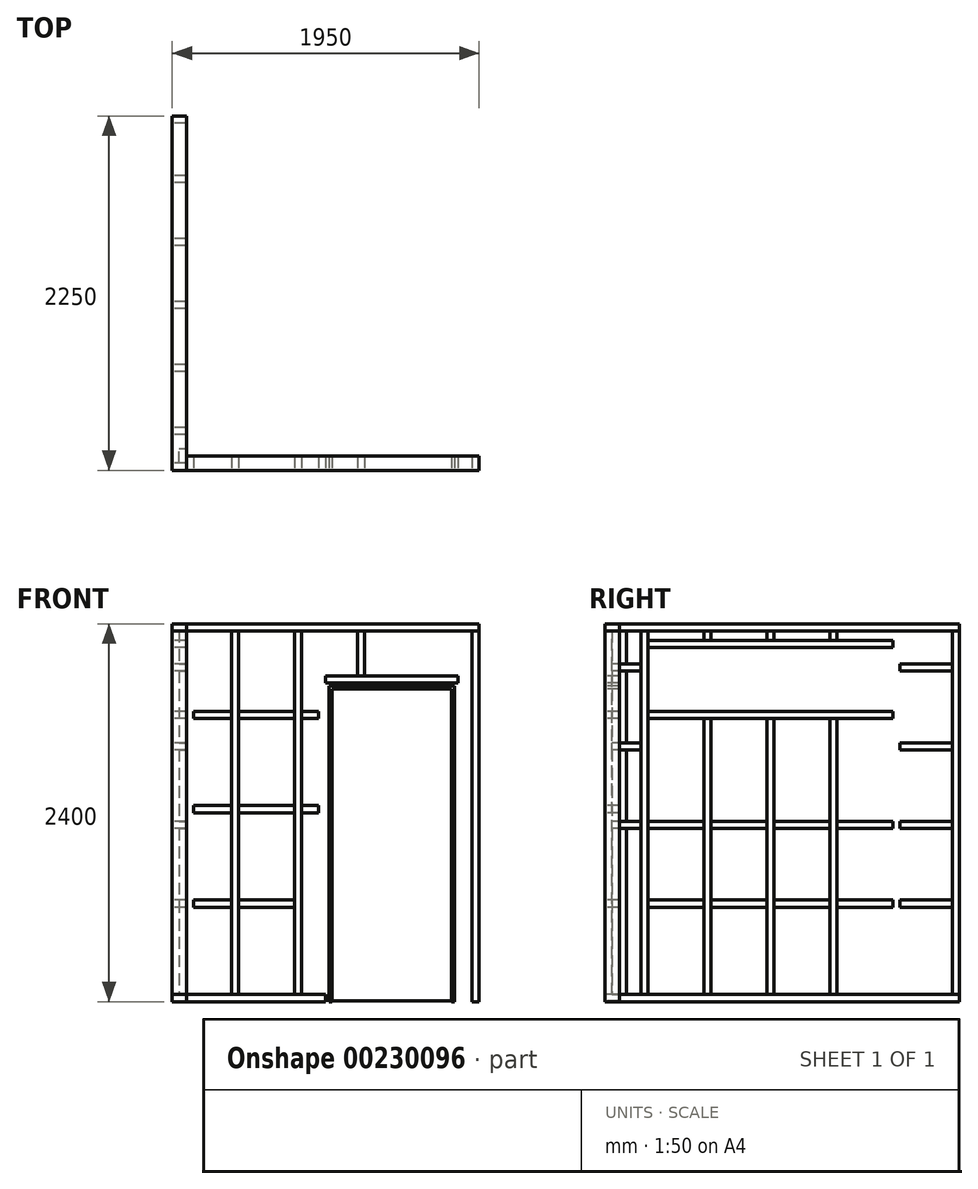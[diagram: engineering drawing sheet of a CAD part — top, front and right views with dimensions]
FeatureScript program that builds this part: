
annotation { "Feature Type Name" : "Feature", "Feature Type Description" : "" }
export const myFeature = defineFeature(function(context is Context, id is Id, definition is map)
    precondition{}
    {
        {
            var Q0;
            Q0=qCreatedBy(makeId("Top.planeOp"),FACE);
            var sketch = newSketch(context, id + "F0", { "sketchPlane" : qUnion([Q0])});
            skLineSegment(sketch, "E0.bottom", {"start": v(-1950, 0) * mm, "end": v(0, 0) * mm});
            skLineSegment(sketch, "E0.top", {"start": v(-1950, -2250) * mm, "end": v(0, -2250) * mm});
            skLineSegment(sketch, "E0.left", {"start": v(-1950, 0) * mm, "end": v(-1950, -2250) * mm});
            skLineSegment(sketch, "E0.right", {"start": v(0, 0) * mm, "end": v(0, -2250) * mm});
            skLineSegment(sketch, "E1.bottom", {"start": v(-1950, 0) * mm, "end": v(-1860, 0) * mm});
            skLineSegment(sketch, "E1.top", {"start": v(-1950, -2250) * mm, "end": v(-1860, -2250) * mm});
            skLineSegment(sketch, "E1.right", {"start": v(-1860, 0) * mm, "end": v(-1860, -2250) * mm});
            skLineSegment(sketch, "E2.bottom", {"start": v(-1860, -2160) * mm, "end": v(0, -2160) * mm});
            skLineSegment(sketch, "E2.top", {"start": v(-1860, -2250) * mm, "end": v(0, -2250) * mm});
            skLineSegment(sketch, "E2.left", {"start": v(-1860, -2160) * mm, "end": v(-1860, -2250) * mm});
            skLineSegment(sketch, "E2.right", {"start": v(0, -2160) * mm, "end": v(0, -2250) * mm});
            skSolve(sketch);
        }
        {
            var Q0;
            Q0=qCreatedBy(makeId("Right.planeOp"),FACE);
            var Q1;
            Q1=sQuery(id+"F0.wireOp",VERTEX,"E0.bottom.start");
            cPlane(context, id + "F1", {"entities" : qUnion([Q0, Q1]), "cplaneType" : CPlaneType.PLANE_POINT, "offset" : 25 * mm, "width" : 150 * mm, "height" : 150 * mm});
        }
        {
            var Q0;
            Q0=qCreatedBy(makeId("Front.planeOp"),FACE);
            var Q1;
            Q1=sQuery(id+"F0.wireOp",VERTEX,"E0.top.end");
            cPlane(context, id + "F2", {"entities" : qUnion([Q0, Q1]), "cplaneType" : CPlaneType.PLANE_POINT, "offset" : 25 * mm, "width" : 150 * mm, "height" : 150 * mm});
        }
        {
            var Q0;
            Q0=qCreatedBy(id+"F1.planeOp",FACE);
            var sketch = newSketch(context, id + "F3", { "sketchPlane" : qUnion([Q0])});
            skLineSegment(sketch, "E3.left", {"start": v(0, 0) * mm, "end": v(0, 2400) * mm});
            skLineSegment(sketch, "E4.0", {"start": v(-45, 45) * mm, "end": v(-45, 2355) * mm});
            skLineSegment(sketch, "E4.2", {"start": v(-2205, 45) * mm, "end": v(-2205, 2355) * mm});
            skLineSegment(sketch, "E5.left", {"start": v(-45, 645) * mm, "end": v(-45, 600) * mm});
            skLineSegment(sketch, "E6", {"start": v(-45, 45) * mm, "end": v(0, 45) * mm});
            skLineSegment(sketch, "E7", {"start": v(0, 2400) * mm, "end": v(-2250, 2400) * mm});
            skLineSegment(sketch, "E8", {"start": v(-45, 2355) * mm, "end": v(-2205, 2355) * mm});
            skLineSegment(sketch, "E9", {"start": v(-45, 2355) * mm, "end": v(0, 2355) * mm});
            skLineSegment(sketch, "E10", {"start": v(-2205, 2355) * mm, "end": v(-2250, 2355) * mm});
            skLineSegment(sketch, "E11", {"start": v(-2250, 0) * mm, "end": v(-2250, 2355) * mm});
            skLineSegment(sketch, "E12", {"start": v(-2250, 2400) * mm, "end": v(-2250, 2355) * mm});
            skLineSegment(sketch, "E13.bottom", {"start": v(-45, 45) * mm, "end": v(-2205, 45) * mm});
            skLineSegment(sketch, "E13.top", {"start": v(0, 0) * mm, "end": v(-2250, 0) * mm});
            skLineSegment(sketch, "E14.bottom", {"start": v(0, 45) * mm, "end": v(-45, 45) * mm});
            skLineSegment(sketch, "E14.left", {"start": v(0, 45) * mm, "end": v(0, 0) * mm});
            skLineSegment(sketch, "E15", {"start": v(-2205, 45) * mm, "end": v(-2250, 45) * mm});
            skLineSegment(sketch, "E16.bottom", {"start": v(-45, 645) * mm, "end": v(-377.5, 645) * mm});
            skLineSegment(sketch, "E16.top", {"start": v(-45, 600) * mm, "end": v(-377.5, 600) * mm});
            skLineSegment(sketch, "E16.right", {"start": v(-2205, 645) * mm, "end": v(-2205, 600) * mm});
            skLineSegment(sketch, "E17.bottom", {"start": v(-377.5, 45) * mm, "end": v(-422.5, 45) * mm});
            skLineSegment(sketch, "E17.top", {"start": v(-377.5, 2355) * mm, "end": v(-422.5, 2355) * mm});
            skLineSegment(sketch, "E17.left", {"start": v(-377.5, 45) * mm, "end": v(-377.5, 2355) * mm});
            skLineSegment(sketch, "E17.right", {"start": v(-422.5, 45) * mm, "end": v(-422.5, 2355) * mm});
            skPoint(sketch, "E18", {"position": v(-400, 45) * mm});
            skPoint(sketch, "E19", {"position": v(0, 45) * mm});
            skLineSegment(sketch, "E20.1.0.0", {"start": v(-777.5, 45) * mm, "end": v(-777.5, 1800) * mm});
            skLineSegment(sketch, "E20.1.0.1", {"start": v(-822.5, 45) * mm, "end": v(-822.5, 1800) * mm});
            skLineSegment(sketch, "E20.2.0.0", {"start": v(-1177.5, 45) * mm, "end": v(-1177.5, 1800) * mm});
            skLineSegment(sketch, "E20.2.0.1", {"start": v(-1222.5, 45) * mm, "end": v(-1222.5, 1800) * mm});
            skLineSegment(sketch, "E20.3.0.0", {"start": v(-1577.5, 45) * mm, "end": v(-1577.5, 1800) * mm});
            skLineSegment(sketch, "E20.3.0.1", {"start": v(-1622.5, 45) * mm, "end": v(-1622.5, 1800) * mm});
            skLineSegment(sketch, "E20.4.0.0", {"start": v(-1977.5, 45) * mm, "end": v(-1977.5, 2355) * mm});
            skLineSegment(sketch, "E20.4.0.1", {"start": v(-2022.5, 45) * mm, "end": v(-2022.5, 2355) * mm});
            skLineSegment(sketch, "E20.direction1", {"start": v(-422.5, 45) * mm, "end": v(-822.5, 45) * mm, "construction": true});
            skLineSegment(sketch, "E21.trimOffspring", {"start": v(-422.5, 645) * mm, "end": v(-777.5, 645) * mm});
            skLineSegment(sketch, "E22.trimOffspring", {"start": v(-422.5, 600) * mm, "end": v(-777.5, 600) * mm});
            skLineSegment(sketch, "E23.trimOffspring", {"start": v(-822.5, 645) * mm, "end": v(-1177.5, 645) * mm});
            skLineSegment(sketch, "E24.trimOffspring", {"start": v(-822.5, 600) * mm, "end": v(-1177.5, 600) * mm});
            skLineSegment(sketch, "E25.trimOffspring", {"start": v(-1222.5, 645) * mm, "end": v(-1577.5, 645) * mm});
            skLineSegment(sketch, "E26.trimOffspring", {"start": v(-1222.5, 600) * mm, "end": v(-1577.5, 600) * mm});
            skLineSegment(sketch, "E27.trimOffspring", {"start": v(-1622.5, 645) * mm, "end": v(-1977.5, 645) * mm});
            skLineSegment(sketch, "E28.trimOffspring", {"start": v(-1622.5, 600) * mm, "end": v(-1977.5, 600) * mm});
            skLineSegment(sketch, "E29.trimOffspring", {"start": v(-2022.5, 645) * mm, "end": v(-2205, 645) * mm});
            skLineSegment(sketch, "E30.trimOffspring", {"start": v(-2022.5, 600) * mm, "end": v(-2205, 600) * mm});
            skLineSegment(sketch, "E31.0.1.0", {"start": v(-822.5, 1100) * mm, "end": v(-1177.5, 1100) * mm});
            skLineSegment(sketch, "E31.0.1.1", {"start": v(-422.5, 1100) * mm, "end": v(-777.5, 1100) * mm});
            skLineSegment(sketch, "E31.0.1.2", {"start": v(-422.5, 1145) * mm, "end": v(-777.5, 1145) * mm});
            skLineSegment(sketch, "E31.0.1.3", {"start": v(-822.5, 1145) * mm, "end": v(-1177.5, 1145) * mm});
            skLineSegment(sketch, "E31.0.1.4", {"start": v(-2022.5, 1145) * mm, "end": v(-2205, 1145) * mm});
            skLineSegment(sketch, "E31.0.1.5", {"start": v(-45, 1145) * mm, "end": v(-377.5, 1145) * mm});
            skLineSegment(sketch, "E31.0.1.6", {"start": v(-1622.5, 1100) * mm, "end": v(-1977.5, 1100) * mm});
            skLineSegment(sketch, "E31.0.1.7", {"start": v(-1222.5, 1100) * mm, "end": v(-1577.5, 1100) * mm});
            skLineSegment(sketch, "E31.0.1.8", {"start": v(-1622.5, 1145) * mm, "end": v(-1977.5, 1145) * mm});
            skLineSegment(sketch, "E31.0.1.9", {"start": v(-1222.5, 1145) * mm, "end": v(-1577.5, 1145) * mm});
            skLineSegment(sketch, "E31.0.1.10", {"start": v(-45, 1100) * mm, "end": v(-377.5, 1100) * mm});
            skLineSegment(sketch, "E31.0.1.11", {"start": v(-2022.5, 1100) * mm, "end": v(-2205, 1100) * mm});
            skLineSegment(sketch, "E31.0.1.12", {"start": v(-2205, 1145) * mm, "end": v(-2205, 1100) * mm});
            skLineSegment(sketch, "E31.0.1.13", {"start": v(-45, 1145) * mm, "end": v(-45, 1100) * mm});
            skLineSegment(sketch, "E31.0.1.14", {"start": v(-45, 1145) * mm, "end": v(-45, 1100) * mm});
            skLineSegment(sketch, "E31.0.2.1", {"start": v(-422.5, 1800) * mm, "end": v(-1977.5, 1800) * mm});
            skLineSegment(sketch, "E31.0.2.2", {"start": v(-422.5, 1845) * mm, "end": v(-1977.5, 1845) * mm});
            skLineSegment(sketch, "E31.0.2.4", {"start": v(-2022.5, 1645) * mm, "end": v(-2205, 1645) * mm});
            skLineSegment(sketch, "E31.0.2.5", {"start": v(-45, 1645) * mm, "end": v(-377.5, 1645) * mm});
            skLineSegment(sketch, "E31.0.2.10", {"start": v(-45, 1600) * mm, "end": v(-377.5, 1600) * mm});
            skLineSegment(sketch, "E31.0.2.11", {"start": v(-2022.5, 1600) * mm, "end": v(-2205, 1600) * mm});
            skLineSegment(sketch, "E31.0.2.12", {"start": v(-2205, 1645) * mm, "end": v(-2205, 1600) * mm});
            skLineSegment(sketch, "E31.0.2.13", {"start": v(-45, 1645) * mm, "end": v(-45, 1600) * mm});
            skLineSegment(sketch, "E31.0.2.14", {"start": v(-45, 1645) * mm, "end": v(-45, 1600) * mm});
            skLineSegment(sketch, "E31.0.3.1", {"start": v(-422.5, 2250) * mm, "end": v(-1977.5, 2250) * mm});
            skLineSegment(sketch, "E31.0.3.2", {"start": v(-422.5, 2295) * mm, "end": v(-1977.5, 2295) * mm});
            skLineSegment(sketch, "E31.0.3.4", {"start": v(-2022.5, 2145) * mm, "end": v(-2205, 2145) * mm});
            skLineSegment(sketch, "E31.0.3.5", {"start": v(-45, 2145) * mm, "end": v(-377.5, 2145) * mm});
            skLineSegment(sketch, "E31.0.3.10", {"start": v(-45, 2100) * mm, "end": v(-377.5, 2100) * mm});
            skLineSegment(sketch, "E31.0.3.11", {"start": v(-2022.5, 2100) * mm, "end": v(-2205, 2100) * mm});
            skLineSegment(sketch, "E31.0.3.12", {"start": v(-2205, 2145) * mm, "end": v(-2205, 2100) * mm});
            skLineSegment(sketch, "E31.0.3.13", {"start": v(-45, 2145) * mm, "end": v(-45, 2100) * mm});
            skLineSegment(sketch, "E31.0.3.14", {"start": v(-45, 2145) * mm, "end": v(-45, 2100) * mm});
            skLineSegment(sketch, "E31.direction2", {"start": v(-2205, 600) * mm, "end": v(-2205, 1100) * mm, "construction": true});
            skLineSegment(sketch, "E32.trimOffspring", {"start": v(-777.5, 2295) * mm, "end": v(-777.5, 2355) * mm});
            skLineSegment(sketch, "E33.trimOffspring", {"start": v(-822.5, 2295) * mm, "end": v(-822.5, 2355) * mm});
            skLineSegment(sketch, "E34.trimOffspring", {"start": v(-1177.5, 2295) * mm, "end": v(-1177.5, 2355) * mm});
            skLineSegment(sketch, "E35.trimOffspring", {"start": v(-1222.5, 2295) * mm, "end": v(-1222.5, 2355) * mm});
            skLineSegment(sketch, "E36.trimOffspring", {"start": v(-1577.5, 2295) * mm, "end": v(-1577.5, 2355) * mm});
            skLineSegment(sketch, "E37.trimOffspring", {"start": v(-1622.5, 2295) * mm, "end": v(-1622.5, 2355) * mm});
            skSolve(sketch);
        }
        {
            var Q0;
            {var subQ0=sQuery(id+"F3.wireOp",EDGE,"E9");Q0=makeQuery(id+"F3.imprint","IMPRINT",FACE,{"disambiguationData":[TD([[makeQuery(id+"F3.imprint","IMPRINT",EDGE,{"derivedFrom":subQ0}),-1.0]])]});}
            var Q1;
            {var subQ8=sQuery(id+"F3.wireOp",EDGE,"E17.bottom");Q1=makeQuery(id+"F3.imprint","IMPRINT",FACE,{"disambiguationData":[TD([[makeQuery(id+"F3.imprint","IMPRINT",EDGE,{"derivedFrom":subQ8}),-1.0]])]});}
            var Q2;
            {var subQ0=sQuery(id+"F3.wireOp",EDGE,"E32.trimOffspring");Q2=makeQuery(id+"F3.imprint","IMPRINT",FACE,{"disambiguationData":[TD([[makeQuery(id+"F3.imprint","IMPRINT",EDGE,{"derivedFrom":subQ0}),1.0]])]});}
            var Q3;
            {var subQ0=sQuery(id+"F3.wireOp",EDGE,"E34.trimOffspring");Q3=makeQuery(id+"F3.imprint","IMPRINT",FACE,{"disambiguationData":[TD([[makeQuery(id+"F3.imprint","IMPRINT",EDGE,{"derivedFrom":subQ0}),1.0]])]});}
            var Q4;
            {var subQ0=sQuery(id+"F3.wireOp",EDGE,"E36.trimOffspring");Q4=makeQuery(id+"F3.imprint","IMPRINT",FACE,{"disambiguationData":[TD([[makeQuery(id+"F3.imprint","IMPRINT",EDGE,{"derivedFrom":subQ0}),1.0]])]});}
            var Q5;
            {var subQ0=sQuery(id+"F3.wireOp",EDGE,"E20.4.0.0");var subQ8=sQuery(id+"F3.wireOp",EDGE,"E8");var subQ9=makeQuery(id+"F3.imprint","INTERSECT",VERTEX,{"derivedFrom":[subQ8,subQ0]});Q5=makeQuery(id+"F3.imprint","IMPRINT",FACE,{"disambiguationData":[TD([[makeQuery(id+"F3.imprint","IMPRINT",EDGE,{"disambiguationData":[TD([[subQ9,-1.0]])],"derivedFrom":subQ8}),1.0]])]});}
            var Q6;
            {var subQ3=sQuery(id+"F3.wireOp",EDGE,"E10");Q6=makeQuery(id+"F3.imprint","IMPRINT",FACE,{"disambiguationData":[TD([[makeQuery(id+"F3.imprint","IMPRINT",EDGE,{"derivedFrom":subQ3}),1.0]])]});}
            var Q7;
            {var subQ5=sQuery(id+"F3.wireOp",EDGE,"E13.bottom");var subQ8=sQuery(id+"F3.wireOp",EDGE,"E20.3.0.0");var subQ12=makeQuery(id+"F3.imprint","INTERSECT",VERTEX,{"derivedFrom":[subQ5,subQ8]});Q7=makeQuery(id+"F3.imprint","IMPRINT",FACE,{"disambiguationData":[TD([[makeQuery(id+"F3.imprint","IMPRINT",EDGE,{"disambiguationData":[TD([[subQ12,-1.0]])],"derivedFrom":subQ5}),-1.0]])]});}
            var Q8;
            {var subQ5=sQuery(id+"F3.wireOp",EDGE,"E13.bottom");var subQ8=sQuery(id+"F3.wireOp",EDGE,"E20.2.0.0");var subQ14=makeQuery(id+"F3.imprint","INTERSECT",VERTEX,{"derivedFrom":[subQ5,subQ8]});Q8=makeQuery(id+"F3.imprint","IMPRINT",FACE,{"disambiguationData":[TD([[makeQuery(id+"F3.imprint","IMPRINT",EDGE,{"disambiguationData":[TD([[subQ14,-1.0]])],"derivedFrom":subQ5}),-1.0]])]});}
            var Q9;
            {var subQ4=sQuery(id+"F3.wireOp",EDGE,"E13.bottom");var subQ7=sQuery(id+"F3.wireOp",EDGE,"E20.1.0.0");var subQ13=makeQuery(id+"F3.imprint","INTERSECT",VERTEX,{"derivedFrom":[subQ4,subQ7]});Q9=makeQuery(id+"F3.imprint","IMPRINT",FACE,{"disambiguationData":[TD([[makeQuery(id+"F3.imprint","IMPRINT",EDGE,{"disambiguationData":[TD([[subQ13,-1.0]])],"derivedFrom":subQ4}),-1.0]])]});}
            extrude(context, id + "F4", {"entities" : qUnion([Q0, Q1, Q2, Q3, Q4, Q5, Q6, Q7, Q8, Q9]), "depth" : 90 * mm, "offsetDistance" : 25 * mm});
        }
        {
            var Q0;
            {var subQ8=sQuery(id+"F3.wireOp",EDGE,"E7");Q0=makeQuery(id+"F3.imprint","IMPRINT",FACE,{"disambiguationData":[TD([[makeQuery(id+"F3.imprint","IMPRINT",EDGE,{"derivedFrom":subQ8}),1.0]])]});}
            var Q1;
            {var subQ0=sQuery(id+"F3.wireOp",EDGE,"E31.0.3.1");Q1=makeQuery(id+"F3.imprint","IMPRINT",FACE,{"disambiguationData":[TD([[makeQuery(id+"F3.imprint","IMPRINT",EDGE,{"derivedFrom":subQ0}),-1.0]])]});}
            var Q2;
            {var subQ0=sQuery(id+"F3.wireOp",EDGE,"E31.0.3.5");Q2=makeQuery(id+"F3.imprint","IMPRINT",FACE,{"disambiguationData":[TD([[makeQuery(id+"F3.imprint","IMPRINT",EDGE,{"derivedFrom":subQ0}),1.0]])]});}
            var Q3;
            {var subQ5=sQuery(id+"F3.wireOp",EDGE,"E31.0.2.2");Q3=makeQuery(id+"F3.imprint","IMPRINT",FACE,{"disambiguationData":[TD([[makeQuery(id+"F3.imprint","IMPRINT",EDGE,{"derivedFrom":subQ5}),1.0]])]});}
            var Q4;
            {var subQ0=sQuery(id+"F3.wireOp",EDGE,"E31.0.2.5");Q4=makeQuery(id+"F3.imprint","IMPRINT",FACE,{"disambiguationData":[TD([[makeQuery(id+"F3.imprint","IMPRINT",EDGE,{"derivedFrom":subQ0}),1.0]])]});}
            var Q5;
            {var subQ0=sQuery(id+"F3.wireOp",EDGE,"E31.0.1.5");Q5=makeQuery(id+"F3.imprint","IMPRINT",FACE,{"disambiguationData":[TD([[makeQuery(id+"F3.imprint","IMPRINT",EDGE,{"derivedFrom":subQ0}),1.0]])]});}
            var Q6;
            {var subQ0=sQuery(id+"F3.wireOp",EDGE,"E31.0.1.1");Q6=makeQuery(id+"F3.imprint","IMPRINT",FACE,{"disambiguationData":[TD([[makeQuery(id+"F3.imprint","IMPRINT",EDGE,{"derivedFrom":subQ0}),-1.0]])]});}
            var Q7;
            {var subQ0=sQuery(id+"F3.wireOp",EDGE,"E31.0.1.0");Q7=makeQuery(id+"F3.imprint","IMPRINT",FACE,{"disambiguationData":[TD([[makeQuery(id+"F3.imprint","IMPRINT",EDGE,{"derivedFrom":subQ0}),-1.0]])]});}
            var Q8;
            {var subQ0=sQuery(id+"F3.wireOp",EDGE,"E31.0.1.7");Q8=makeQuery(id+"F3.imprint","IMPRINT",FACE,{"disambiguationData":[TD([[makeQuery(id+"F3.imprint","IMPRINT",EDGE,{"derivedFrom":subQ0}),-1.0]])]});}
            var Q9;
            {var subQ0=sQuery(id+"F3.wireOp",EDGE,"E31.0.1.6");Q9=makeQuery(id+"F3.imprint","IMPRINT",FACE,{"disambiguationData":[TD([[makeQuery(id+"F3.imprint","IMPRINT",EDGE,{"derivedFrom":subQ0}),-1.0]])]});}
            var Q10;
            {var subQ0=sQuery(id+"F3.wireOp",EDGE,"E31.0.1.4");Q10=makeQuery(id+"F3.imprint","IMPRINT",FACE,{"disambiguationData":[TD([[makeQuery(id+"F3.imprint","IMPRINT",EDGE,{"derivedFrom":subQ0}),1.0]])]});}
            var Q11;
            Q11=makeQuery(id+"F3.imprint","IMPRINT",FACE,{"disambiguationData":[TD([[makeQuery(id+"F3.imprint","IMPRINT",EDGE,{"derivedFrom":sQuery(id+"F3.wireOp",EDGE,"E16.right")}),1.0]])]});
            var Q12;
            {var subQ0=sQuery(id+"F3.wireOp",EDGE,"E27.trimOffspring");Q12=makeQuery(id+"F3.imprint","IMPRINT",FACE,{"disambiguationData":[TD([[makeQuery(id+"F3.imprint","IMPRINT",EDGE,{"derivedFrom":subQ0}),1.0]])]});}
            var Q13;
            {var subQ0=sQuery(id+"F3.wireOp",EDGE,"E25.trimOffspring");Q13=makeQuery(id+"F3.imprint","IMPRINT",FACE,{"disambiguationData":[TD([[makeQuery(id+"F3.imprint","IMPRINT",EDGE,{"derivedFrom":subQ0}),1.0]])]});}
            var Q14;
            {var subQ0=sQuery(id+"F3.wireOp",EDGE,"E23.trimOffspring");Q14=makeQuery(id+"F3.imprint","IMPRINT",FACE,{"disambiguationData":[TD([[makeQuery(id+"F3.imprint","IMPRINT",EDGE,{"derivedFrom":subQ0}),1.0]])]});}
            var Q15;
            {var subQ0=sQuery(id+"F3.wireOp",EDGE,"E21.trimOffspring");Q15=makeQuery(id+"F3.imprint","IMPRINT",FACE,{"disambiguationData":[TD([[makeQuery(id+"F3.imprint","IMPRINT",EDGE,{"derivedFrom":subQ0}),1.0]])]});}
            var Q16;
            {var subQ0=sQuery(id+"F3.wireOp",EDGE,"E16.bottom");Q16=makeQuery(id+"F3.imprint","IMPRINT",FACE,{"disambiguationData":[TD([[makeQuery(id+"F3.imprint","IMPRINT",EDGE,{"derivedFrom":subQ0}),1.0]])]});}
            var Q17;
            {var subQ8=sQuery(id+"F3.wireOp",EDGE,"E13.top");Q17=makeQuery(id+"F3.imprint","IMPRINT",FACE,{"disambiguationData":[TD([[makeQuery(id+"F3.imprint","IMPRINT",EDGE,{"derivedFrom":subQ8}),-1.0]])]});}
            var Q18;
            {var subQ0=sQuery(id+"F3.wireOp",EDGE,"E31.0.2.4");Q18=makeQuery(id+"F3.imprint","IMPRINT",FACE,{"disambiguationData":[TD([[makeQuery(id+"F3.imprint","IMPRINT",EDGE,{"derivedFrom":subQ0}),1.0]])]});}
            var Q19;
            {var subQ0=sQuery(id+"F3.wireOp",EDGE,"E31.0.3.4");Q19=makeQuery(id+"F3.imprint","IMPRINT",FACE,{"disambiguationData":[TD([[makeQuery(id+"F3.imprint","IMPRINT",EDGE,{"derivedFrom":subQ0}),1.0]])]});}
            extrude(context, id + "F5", {"entities" : qUnion([Q0, Q1, Q2, Q3, Q4, Q5, Q6, Q7, Q8, Q9, Q10, Q11, Q12, Q13, Q14, Q15, Q16, Q17, Q18, Q19]), "depth" : 90 * mm, "offsetDistance" : 25 * mm});
        }
        {
            var Q0;
            Q0=qCreatedBy(id+"F2.planeOp",FACE);
            var sketch = newSketch(context, id + "F6", { "sketchPlane" : qUnion([Q0])});
            skLineSegment(sketch, "E38.bottom", {"start": v(-1860, 2400) * mm, "end": v(0, 2400) * mm});
            skLineSegment(sketch, "E38.left", {"start": v(-1860, 2400) * mm, "end": v(-1860, 0) * mm});
            skLineSegment(sketch, "E39.left", {"start": v(-1860, 45) * mm, "end": v(-1860, 0) * mm});
            skLineSegment(sketch, "E40.trimOffspring", {"start": v(-1860, 2355) * mm, "end": v(0, 2355) * mm});
            skLineSegment(sketch, "E41.bottom", {"start": v(-1860, 2355) * mm, "end": v(-1815, 2355) * mm});
            skLineSegment(sketch, "E41.top", {"start": v(-1860, 45) * mm, "end": v(-1815, 45) * mm});
            skLineSegment(sketch, "E41.left", {"start": v(-1860, 2355) * mm, "end": v(-1860, 45) * mm});
            skLineSegment(sketch, "E41.right", {"start": v(-1815, 2355) * mm, "end": v(-1815, 45) * mm});
            skLineSegment(sketch, "E42.right", {"start": v(0, 0) * mm, "end": v(0, 2400) * mm});
            skLineSegment(sketch, "E43.MirrorCS", {"start": v(-135, 2355) * mm, "end": v(-90, 2355) * mm});
            skLineSegment(sketch, "E44.MirrorCS", {"start": v(-975, 45) * mm, "end": v(-975, 0) * mm});
            skLineSegment(sketch, "E45.MirrorCS", {"start": v(-45, 0) * mm, "end": v(0, 0) * mm});
            skLineSegment(sketch, "E46.MirrorCS", {"start": v(-175, 45) * mm, "end": v(-175, 1985) * mm});
            skLineSegment(sketch, "E47.MirrorCS", {"start": v(-935, 0) * mm, "end": v(-935, 1985) * mm});
            skLineSegment(sketch, "E48.MirrorCS", {"start": v(-935, 1985) * mm, "end": v(-175, 1985) * mm});
            skLineSegment(sketch, "E49.MirrorCS", {"start": v(-955, 2005) * mm, "end": v(-955, 0) * mm});
            skLineSegment(sketch, "E50.MirrorCS", {"start": v(-935, 1985) * mm, "end": v(-935, 45) * mm});
            skLineSegment(sketch, "E51.MirrorCS", {"start": v(-135, 2355) * mm, "end": v(-135, 2025) * mm});
            skLineSegment(sketch, "E52.MirrorCS", {"start": v(-175, 1985) * mm, "end": v(-935, 1985) * mm});
            skLineSegment(sketch, "E53.MirrorCS", {"start": v(-955, 2005) * mm, "end": v(-156.87, 2005) * mm});
            skLineSegment(sketch, "E54.MirrorCS", {"start": v(-90, 2355) * mm, "end": v(-90, 0) * mm});
            skLineSegment(sketch, "E55.MirrorCS", {"start": v(-975, 2355) * mm, "end": v(-975, 45) * mm});
            skLineSegment(sketch, "E56.MirrorCS", {"start": v(-175, 1985) * mm, "end": v(-175, 0) * mm});
            skLineSegment(sketch, "E57.MirrorCS", {"start": v(-45, 0) * mm, "end": v(-45, 2355) * mm});
            skLineSegment(sketch, "E58.MirrorCS", {"start": v(-45, 0) * mm, "end": v(-135, 0) * mm});
            skLineSegment(sketch, "E59.bottom", {"start": v(-1860, 45) * mm, "end": v(-975, 45) * mm});
            skLineSegment(sketch, "E59.top", {"start": v(-1860, 0) * mm, "end": v(-975, 0) * mm});
            skLineSegment(sketch, "E60.top", {"start": v(-135, 2355) * mm, "end": v(-1815, 2355) * mm});
            skLineSegment(sketch, "E60.left", {"start": v(-135, 2355) * mm, "end": v(-135, 45.5) * mm});
            skLineSegment(sketch, "E61.bottom", {"start": v(-975, 45) * mm, "end": v(-1020, 45) * mm});
            skLineSegment(sketch, "E61.top", {"start": v(-975, 2355) * mm, "end": v(-1020, 2355) * mm});
            skLineSegment(sketch, "E61.left", {"start": v(-975, 45) * mm, "end": v(-975, 2355) * mm});
            skLineSegment(sketch, "E61.right", {"start": v(-1020, 45) * mm, "end": v(-1020, 2355) * mm});
            skLineSegment(sketch, "E62.bottom", {"start": v(-1172.5, 2355) * mm, "end": v(-1127.5, 2355) * mm});
            skLineSegment(sketch, "E63", {"start": v(-135, 2025) * mm, "end": v(-135, 0) * mm});
            skPoint(sketch, "E64.orphan", {"position": v(-175, 0) * mm});
            skLineSegment(sketch, "E65", {"start": v(-156.87, 2005) * mm, "end": v(-156.87, 0) * mm});
            skLineSegment(sketch, "E66", {"start": v(-175, 0) * mm, "end": v(-156.87, 0) * mm});
            skLineSegment(sketch, "E67", {"start": v(-955, 0) * mm, "end": v(-935, 0) * mm});
            skLineSegment(sketch, "E68.bottom", {"start": v(-90, 0) * mm, "end": v(-45, 0) * mm});
            skLineSegment(sketch, "E68.top", {"start": v(-90, 150) * mm, "end": v(-45, 150) * mm});
            skLineSegment(sketch, "E68.left", {"start": v(-90, 0) * mm, "end": v(-90, 150) * mm});
            skLineSegment(sketch, "E68.right", {"start": v(-45, 0) * mm, "end": v(-45, 150) * mm});
            skLineSegment(sketch, "E69.0.1.0", {"start": v(-90, 550) * mm, "end": v(-90, 700) * mm});
            skLineSegment(sketch, "E69.0.1.1", {"start": v(-90, 550) * mm, "end": v(-45, 550) * mm});
            skLineSegment(sketch, "E69.0.1.2", {"start": v(-45, 550) * mm, "end": v(-45, 700) * mm});
            skLineSegment(sketch, "E69.0.1.3", {"start": v(-90, 700) * mm, "end": v(-45, 700) * mm});
            skLineSegment(sketch, "E69.0.2.0", {"start": v(-90, 1100) * mm, "end": v(-90, 1250) * mm});
            skLineSegment(sketch, "E69.0.2.1", {"start": v(-90, 1100) * mm, "end": v(-45, 1100) * mm});
            skLineSegment(sketch, "E69.0.2.2", {"start": v(-45, 1100) * mm, "end": v(-45, 1250) * mm});
            skLineSegment(sketch, "E69.0.2.3", {"start": v(-90, 1250) * mm, "end": v(-45, 1250) * mm});
            skLineSegment(sketch, "E69.0.3.0", {"start": v(-90, 1650) * mm, "end": v(-90, 1800) * mm});
            skLineSegment(sketch, "E69.0.3.1", {"start": v(-90, 1650) * mm, "end": v(-45, 1650) * mm});
            skLineSegment(sketch, "E69.0.3.2", {"start": v(-45, 1650) * mm, "end": v(-45, 1800) * mm});
            skLineSegment(sketch, "E69.0.3.3", {"start": v(-90, 1800) * mm, "end": v(-45, 1800) * mm});
            skLineSegment(sketch, "E69.0.4.0", {"start": v(-90, 2200) * mm, "end": v(-90, 2350) * mm});
            skLineSegment(sketch, "E69.0.4.1", {"start": v(-90, 2200) * mm, "end": v(-45, 2200) * mm});
            skLineSegment(sketch, "E69.0.4.2", {"start": v(-45, 2200) * mm, "end": v(-45, 2350) * mm});
            skLineSegment(sketch, "E69.0.4.3", {"start": v(-90, 2350) * mm, "end": v(-45, 2350) * mm});
            skLineSegment(sketch, "E69.direction1", {"start": v(-90, 0) * mm, "end": v(-65, 0) * mm, "construction": true});
            skLineSegment(sketch, "E69.direction2", {"start": v(-90, 0) * mm, "end": v(-90, 550) * mm, "construction": true});
            skLineSegment(sketch, "E70.bottom", {"start": v(-372.5, 2355) * mm, "end": v(-327.5, 2355) * mm});
            skLineSegment(sketch, "E70.left", {"start": v(-372.5, 2355) * mm, "end": v(-372.5, 2070) * mm});
            skLineSegment(sketch, "E70.right", {"start": v(-327.5, 2355) * mm, "end": v(-327.5, 2070) * mm});
            skPoint(sketch, "E71", {"position": v(-350, 2355) * mm});
            skLineSegment(sketch, "E72.1.0.0", {"start": v(-727.5, 2355) * mm, "end": v(-727.5, 2070) * mm});
            skPoint(sketch, "E72.1.0.2", {"position": v(-750, 2355) * mm});
            skLineSegment(sketch, "E72.1.0.3", {"start": v(-772.5, 2355) * mm, "end": v(-772.5, 2070) * mm});
            skPoint(sketch, "E72.1.0.4", {"position": v(-750, 2355) * mm});
            skLineSegment(sketch, "E72.1.0.5", {"start": v(-772.5, 2355) * mm, "end": v(-727.5, 2355) * mm});
            skLineSegment(sketch, "E72.2.0.0", {"start": v(-1127.5, 2355) * mm, "end": v(-1127.5, 45) * mm});
            skLineSegment(sketch, "E72.2.0.1", {"start": v(-1172.5, 45) * mm, "end": v(-1127.5, 45) * mm});
            skPoint(sketch, "E72.2.0.2", {"position": v(-1150, 2355) * mm});
            skLineSegment(sketch, "E72.2.0.3", {"start": v(-1172.5, 2355) * mm, "end": v(-1172.5, 45) * mm});
            skPoint(sketch, "E72.2.0.4", {"position": v(-1150, 2355) * mm});
            skLineSegment(sketch, "E72.3.0.0", {"start": v(-1527.5, 2355) * mm, "end": v(-1527.5, 45) * mm});
            skLineSegment(sketch, "E72.3.0.1", {"start": v(-1572.5, 45) * mm, "end": v(-1527.5, 45) * mm});
            skPoint(sketch, "E72.3.0.2", {"position": v(-1550, 2355) * mm});
            skLineSegment(sketch, "E72.3.0.3", {"start": v(-1572.5, 2355) * mm, "end": v(-1572.5, 45) * mm});
            skPoint(sketch, "E72.3.0.4", {"position": v(-1550, 2355) * mm});
            skLineSegment(sketch, "E72.3.0.5", {"start": v(-1572.5, 2355) * mm, "end": v(-1527.5, 2355) * mm});
            skLineSegment(sketch, "E73", {"start": v(-135, 2025) * mm, "end": v(-975, 2025) * mm});
            skLineSegment(sketch, "E74.trimOffspring", {"start": v(-1127.5, 45) * mm, "end": v(-1172.5, 45) * mm});
            skLineSegment(sketch, "E75.trimOffspring", {"start": v(-1527.5, 45) * mm, "end": v(-1572.5, 45) * mm});
            skLineSegment(sketch, "E76", {"start": v(-135, 2070) * mm, "end": v(-975, 2070) * mm});
            skLineSegment(sketch, "E77.bottom", {"start": v(-1815, 645) * mm, "end": v(-1572.5, 645) * mm});
            skLineSegment(sketch, "E77.top", {"start": v(-1815, 600) * mm, "end": v(-1572.5, 600) * mm});
            skLineSegment(sketch, "E77.left", {"start": v(-1815, 645) * mm, "end": v(-1815, 600) * mm});
            skLineSegment(sketch, "E77.right", {"start": v(-1020, 645) * mm, "end": v(-1020, 600) * mm});
            skLineSegment(sketch, "E78.trimOffspring", {"start": v(-1527.5, 645) * mm, "end": v(-1172.5, 645) * mm});
            skLineSegment(sketch, "E79.trimOffspring", {"start": v(-1527.5, 600) * mm, "end": v(-1172.5, 600) * mm});
            skLineSegment(sketch, "E80.trimOffspring", {"start": v(-1127.5, 645) * mm, "end": v(-1020, 645) * mm});
            skLineSegment(sketch, "E81.trimOffspring", {"start": v(-1127.5, 600) * mm, "end": v(-1020, 600) * mm});
            skLineSegment(sketch, "E82.0.1.0", {"start": v(-1815, 1245) * mm, "end": v(-1572.5, 1245) * mm});
            skLineSegment(sketch, "E82.0.1.1", {"start": v(-1815, 1200) * mm, "end": v(-1572.5, 1200) * mm});
            skLineSegment(sketch, "E82.0.1.2", {"start": v(-1527.5, 1245) * mm, "end": v(-1172.5, 1245) * mm});
            skLineSegment(sketch, "E82.0.1.3", {"start": v(-1527.5, 1200) * mm, "end": v(-1172.5, 1200) * mm});
            skLineSegment(sketch, "E82.0.1.4", {"start": v(-1127.5, 1245) * mm, "end": v(-1020, 1245) * mm});
            skLineSegment(sketch, "E82.0.1.5", {"start": v(-1127.5, 1200) * mm, "end": v(-1020, 1200) * mm});
            skLineSegment(sketch, "E82.0.2.0", {"start": v(-1815, 1845) * mm, "end": v(-1572.5, 1845) * mm});
            skLineSegment(sketch, "E82.0.2.1", {"start": v(-1815, 1800) * mm, "end": v(-1572.5, 1800) * mm});
            skLineSegment(sketch, "E82.0.2.2", {"start": v(-1527.5, 1845) * mm, "end": v(-1172.5, 1845) * mm});
            skLineSegment(sketch, "E82.0.2.3", {"start": v(-1527.5, 1800) * mm, "end": v(-1172.5, 1800) * mm});
            skLineSegment(sketch, "E82.0.2.4", {"start": v(-1127.5, 1845) * mm, "end": v(-1020, 1845) * mm});
            skLineSegment(sketch, "E82.0.2.5", {"start": v(-1127.5, 1800) * mm, "end": v(-1020, 1800) * mm});
            skLineSegment(sketch, "E82.direction1", {"start": v(-1815, 645) * mm, "end": v(-1790, 645) * mm, "construction": true});
            skLineSegment(sketch, "E82.direction2", {"start": v(-1815, 645) * mm, "end": v(-1815, 1245) * mm, "construction": true});
            skLineSegment(sketch, "E83.trimOffspring", {"start": v(-156.87, 0) * mm, "end": v(-935, 0) * mm});
            skLineSegment(sketch, "E84.bottom", {"start": v(-935, 0) * mm, "end": v(-175, 0) * mm});
            skLineSegment(sketch, "E84.top", {"start": v(-935, 5) * mm, "end": v(-175, 5) * mm});
            skLineSegment(sketch, "E84.left", {"start": v(-935, 0) * mm, "end": v(-935, 5) * mm});
            skLineSegment(sketch, "E84.right", {"start": v(-175, 0) * mm, "end": v(-175, 5) * mm});
            skSolve(sketch);
        }
        {
            var Q0;
            Q0=makeQuery(id+"F6.imprint","IMPRINT",FACE,{"disambiguationData":[TD([[makeQuery(id+"F6.imprint","IMPRINT",EDGE,{"derivedFrom":sQuery(id+"F6.wireOp",EDGE,"E41.bottom")}),-1.0]])]});
            var Q1;
            Q1=makeQuery(id+"F6.imprint","IMPRINT",FACE,{"disambiguationData":[TD([[makeQuery(id+"F6.imprint","IMPRINT",EDGE,{"derivedFrom":sQuery(id+"F6.wireOp",EDGE,"E72.3.0.0")}),-1.0]])]});
            var Q2;
            Q2=makeQuery(id+"F6.imprint","IMPRINT",FACE,{"disambiguationData":[TD([[makeQuery(id+"F6.imprint","IMPRINT",EDGE,{"derivedFrom":sQuery(id+"F6.wireOp",EDGE,"E72.2.0.0")}),-1.0]])]});
            var Q3;
            {var subQ0=sQuery(id+"F6.wireOp",EDGE,"E72.1.0.0");Q3=makeQuery(id+"F6.imprint","IMPRINT",FACE,{"disambiguationData":[TD([[makeQuery(id+"F6.imprint","IMPRINT",EDGE,{"derivedFrom":subQ0}),-1.0]])]});}
            var Q4;
            Q4=makeQuery(id+"F6.imprint","IMPRINT",FACE,{"disambiguationData":[TD([[makeQuery(id+"F6.imprint","IMPRINT",EDGE,{"derivedFrom":sQuery(id+"F6.wireOp",EDGE,"E70.bottom")}),-1.0]])]});
            var Q5;
            {var subQ4=sQuery(id+"F6.wireOp",EDGE,"E43.MirrorCS");Q5=makeQuery(id+"F6.imprint","IMPRINT",FACE,{"disambiguationData":[TD([[makeQuery(id+"F6.imprint","IMPRINT",EDGE,{"derivedFrom":subQ4}),-1.0]])]});}
            var Q6;
            {var subQ10=sQuery(id+"F6.wireOp",EDGE,"E45.MirrorCS");Q6=makeQuery(id+"F6.imprint","IMPRINT",FACE,{"disambiguationData":[TD([[makeQuery(id+"F6.imprint","IMPRINT",EDGE,{"derivedFrom":subQ10}),1.0]])]});}
            var Q7;
            {var subQ3=sQuery(id+"F6.wireOp",EDGE,"E61.bottom");Q7=makeQuery(id+"F6.imprint","IMPRINT",FACE,{"disambiguationData":[TD([[makeQuery(id+"F6.imprint","IMPRINT",EDGE,{"derivedFrom":subQ3}),-1.0]])]});}
            var Q8;
            Q8=makeQuery(id+"F6.imprint","IMPRINT",FACE,{"disambiguationData":[TD([[makeQuery(id+"F6.imprint","IMPRINT",EDGE,{"derivedFrom":sQuery(id+"F6.wireOp",EDGE,"E47.MirrorCS")}),-1.0]])]});
            extrude(context, id + "F7", {"entities" : qUnion([Q0, Q1, Q2, Q3, Q4, Q5, Q6, Q7, Q8]), "oppositeDirection" : true, "depth" : 90 * mm, "offsetDistance" : 25 * mm});
        }
        {
            var Q0;
            {var subQ5=sQuery(id+"F6.wireOp",EDGE,"E38.bottom");Q0=makeQuery(id+"F6.imprint","IMPRINT",FACE,{"disambiguationData":[TD([[makeQuery(id+"F6.imprint","IMPRINT",EDGE,{"derivedFrom":subQ5}),-1.0]])]});}
            var Q1;
            {var subQ4=sQuery(id+"F6.wireOp",EDGE,"E73");Q1=makeQuery(id+"F6.imprint","IMPRINT",FACE,{"disambiguationData":[TD([[makeQuery(id+"F6.imprint","IMPRINT",EDGE,{"derivedFrom":subQ4}),-1.0]])]});}
            var Q2;
            Q2=makeQuery(id+"F6.imprint","IMPRINT",FACE,{"disambiguationData":[TD([[makeQuery(id+"F6.imprint","IMPRINT",EDGE,{"derivedFrom":sQuery(id+"F6.wireOp",EDGE,"E59.top")}),1.0]])]});
            var Q3;
            Q3=makeQuery(id+"F6.imprint","IMPRINT",FACE,{"disambiguationData":[TD([[makeQuery(id+"F6.imprint","IMPRINT",EDGE,{"derivedFrom":sQuery(id+"F6.wireOp",EDGE,"E69.0.4.0")}),-1.0]])]});
            var Q4;
            Q4=makeQuery(id+"F6.imprint","IMPRINT",FACE,{"disambiguationData":[TD([[makeQuery(id+"F6.imprint","IMPRINT",EDGE,{"derivedFrom":sQuery(id+"F6.wireOp",EDGE,"E69.0.3.0")}),-1.0]])]});
            var Q5;
            Q5=makeQuery(id+"F6.imprint","IMPRINT",FACE,{"disambiguationData":[TD([[makeQuery(id+"F6.imprint","IMPRINT",EDGE,{"derivedFrom":sQuery(id+"F6.wireOp",EDGE,"E69.0.2.0")}),-1.0]])]});
            var Q6;
            Q6=makeQuery(id+"F6.imprint","IMPRINT",FACE,{"disambiguationData":[TD([[makeQuery(id+"F6.imprint","IMPRINT",EDGE,{"derivedFrom":sQuery(id+"F6.wireOp",EDGE,"E69.0.1.0")}),-1.0]])]});
            var Q7;
            Q7=makeQuery(id+"F6.imprint","IMPRINT",FACE,{"disambiguationData":[TD([[makeQuery(id+"F6.imprint","IMPRINT",EDGE,{"derivedFrom":sQuery(id+"F6.wireOp",EDGE,"E68.bottom")}),1.0]])]});
            var Q8;
            {var subQ0=sQuery(id+"F6.wireOp",EDGE,"E77.bottom");Q8=makeQuery(id+"F6.imprint","IMPRINT",FACE,{"disambiguationData":[TD([[makeQuery(id+"F6.imprint","IMPRINT",EDGE,{"derivedFrom":subQ0}),-1.0]])]});}
            var Q9;
            {var subQ0=sQuery(id+"F6.wireOp",EDGE,"E78.trimOffspring");Q9=makeQuery(id+"F6.imprint","IMPRINT",FACE,{"disambiguationData":[TD([[makeQuery(id+"F6.imprint","IMPRINT",EDGE,{"derivedFrom":subQ0}),-1.0]])]});}
            var Q10;
            Q10=makeQuery(id+"F6.imprint","IMPRINT",FACE,{"disambiguationData":[TD([[makeQuery(id+"F6.imprint","IMPRINT",EDGE,{"derivedFrom":sQuery(id+"F6.wireOp",EDGE,"E77.right")}),-1.0]])]});
            var Q11;
            {var subQ0=sQuery(id+"F6.wireOp",EDGE,"E82.0.1.4");Q11=makeQuery(id+"F6.imprint","IMPRINT",FACE,{"disambiguationData":[TD([[makeQuery(id+"F6.imprint","IMPRINT",EDGE,{"derivedFrom":subQ0}),-1.0]])]});}
            var Q12;
            {var subQ0=sQuery(id+"F6.wireOp",EDGE,"E82.0.1.2");Q12=makeQuery(id+"F6.imprint","IMPRINT",FACE,{"disambiguationData":[TD([[makeQuery(id+"F6.imprint","IMPRINT",EDGE,{"derivedFrom":subQ0}),-1.0]])]});}
            var Q13;
            {var subQ0=sQuery(id+"F6.wireOp",EDGE,"E82.0.1.0");Q13=makeQuery(id+"F6.imprint","IMPRINT",FACE,{"disambiguationData":[TD([[makeQuery(id+"F6.imprint","IMPRINT",EDGE,{"derivedFrom":subQ0}),-1.0]])]});}
            var Q14;
            {var subQ0=sQuery(id+"F6.wireOp",EDGE,"E82.0.2.0");Q14=makeQuery(id+"F6.imprint","IMPRINT",FACE,{"disambiguationData":[TD([[makeQuery(id+"F6.imprint","IMPRINT",EDGE,{"derivedFrom":subQ0}),-1.0]])]});}
            var Q15;
            {var subQ0=sQuery(id+"F6.wireOp",EDGE,"E82.0.2.2");Q15=makeQuery(id+"F6.imprint","IMPRINT",FACE,{"disambiguationData":[TD([[makeQuery(id+"F6.imprint","IMPRINT",EDGE,{"derivedFrom":subQ0}),-1.0]])]});}
            var Q16;
            {var subQ0=sQuery(id+"F6.wireOp",EDGE,"E82.0.2.4");Q16=makeQuery(id+"F6.imprint","IMPRINT",FACE,{"disambiguationData":[TD([[makeQuery(id+"F6.imprint","IMPRINT",EDGE,{"derivedFrom":subQ0}),-1.0]])]});}
            var Q17;
            Q17=makeQuery(id+"F6.imprint","IMPRINT",FACE,{"disambiguationData":[TD([[makeQuery(id+"F6.imprint","IMPRINT",EDGE,{"derivedFrom":sQuery(id+"F6.wireOp",EDGE,"E47.MirrorCS")}),1.0]])]});
            extrude(context, id + "F8", {"entities" : qUnion([Q0, Q1, Q2, Q3, Q4, Q5, Q6, Q7, Q8, Q9, Q10, Q11, Q12, Q13, Q14, Q15, Q16, Q17]), "oppositeDirection" : true, "depth" : 90 * mm, "offsetDistance" : 25 * mm});
        }
        {
            var Q0;
            Q0=makeQuery(id+"F5.opExtrude","SWEPT_FACE",FACE,{"disambiguationData":[OSD([sQuery(id+"F3.wireOp",EDGE,"E13.bottom"),sQuery(id+"F3.wireOp",EDGE,"E14.bottom"),sQuery(id+"F3.wireOp",EDGE,"E15"),sQuery(id+"F3.wireOp",EDGE,"E17.bottom")])]});
            var sketch = newSketch(context, id + "F9", { "sketchPlane" : qUnion([Q0])});
            skLineSegment(sketch, "E85.bottom", {"start": v(-1860, -2205) * mm, "end": v(-1905, -2205) * mm});
            skLineSegment(sketch, "E85.top", {"start": v(-1860, -2115) * mm, "end": v(-1905, -2115) * mm});
            skLineSegment(sketch, "E85.left", {"start": v(-1860, -2205) * mm, "end": v(-1860, -2115) * mm});
            skLineSegment(sketch, "E85.right", {"start": v(-1905, -2205) * mm, "end": v(-1905, -2115) * mm});
            skSolve(sketch);
        }
        {
            var Q0;
            Q0=makeQuery(id+"F9.imprint","IMPRINT",FACE,{"disambiguationData":[TD([[makeQuery(id+"F9.imprint","IMPRINT",EDGE,{"derivedFrom":sQuery(id+"F9.wireOp",EDGE,"E85.bottom")}),-1.0]])]});
            var Q1;
            Q1=makeQuery(id+"F5.opExtrude","SWEPT_FACE",FACE,{"disambiguationData":[OSD([sQuery(id+"F3.wireOp",EDGE,"E8"),sQuery(id+"F3.wireOp",EDGE,"E9"),sQuery(id+"F3.wireOp",EDGE,"E10"),sQuery(id+"F3.wireOp",EDGE,"E17.top")])]});
            extrude(context, id + "F10", {"entities" : qUnion([Q0]), "endBound" : BoundingType.UP_TO_SURFACE, "depth" : 25 * mm, "endBoundEntityFace" : qUnion([Q1]), "offsetDistance" : 25 * mm});
        }
        {
            var Q0;
            Q0=makeQuery(id+"F5.opExtrude","SWEPT_BODY",BODY,{"disambiguationData":[OSD([sQuery(id+"F3.wireOp",EDGE,"E20.4.0.1"),sQuery(id+"F3.wireOp",EDGE,"E31.0.3.4"),sQuery(id+"F3.wireOp",EDGE,"E31.0.3.11"),sQuery(id+"F3.wireOp",EDGE,"E31.0.3.12")])]});
            var Q1;
            Q1=makeQuery(id+"F5.opExtrude","SWEPT_BODY",BODY,{"disambiguationData":[OSD([sQuery(id+"F3.wireOp",EDGE,"E20.4.0.1"),sQuery(id+"F3.wireOp",EDGE,"E31.0.2.4"),sQuery(id+"F3.wireOp",EDGE,"E31.0.2.11"),sQuery(id+"F3.wireOp",EDGE,"E31.0.2.12")])]});
            var Q2;
            Q2=makeQuery(id+"F5.opExtrude","SWEPT_BODY",BODY,{"disambiguationData":[OSD([sQuery(id+"F3.wireOp",EDGE,"E20.4.0.1"),sQuery(id+"F3.wireOp",EDGE,"E31.0.1.4"),sQuery(id+"F3.wireOp",EDGE,"E31.0.1.11"),sQuery(id+"F3.wireOp",EDGE,"E31.0.1.12")])]});
            var Q3;
            Q3=makeQuery(id+"F5.opExtrude","SWEPT_BODY",BODY,{"disambiguationData":[OSD([sQuery(id+"F3.wireOp",EDGE,"E16.right"),sQuery(id+"F3.wireOp",EDGE,"E20.4.0.1"),sQuery(id+"F3.wireOp",EDGE,"E29.trimOffspring"),sQuery(id+"F3.wireOp",EDGE,"E30.trimOffspring")])]});
            var Q4;
            Q4=makeQuery(id+"F10.opExtrude","SWEPT_BODY",BODY,{"disambiguationData":[OSD([sQuery(id+"F9.wireOp",EDGE,"E85.bottom"),sQuery(id+"F9.wireOp",EDGE,"E85.top"),sQuery(id+"F9.wireOp",EDGE,"E85.left"),sQuery(id+"F9.wireOp",EDGE,"E85.right")])]});
            booleanBodies(context, id + "F11", {"operationType" : BooleanOperationType.SUBTRACTION, "tools" : qUnion([Q0, Q1, Q2, Q3]), "targets" : qUnion([Q4]), "keepTools" : true});
        }
    });
